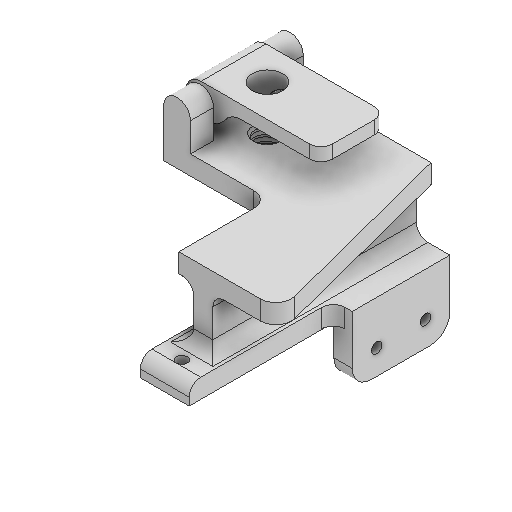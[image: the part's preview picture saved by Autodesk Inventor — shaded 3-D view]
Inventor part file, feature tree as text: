
AUTODESK INVENTOR PART (.ipt)
format: ipt  version: 2025 (Build 290162000, 162)  size: 534,016 bytes
history: native  units: mm
features: sketch x20, extrude x19, projected_geometry x18, fillet x7, plane x6, mirror x1, helix x1
ambient origin geometry x8: Origin, YZ Plane, XZ Plane, XY Plane, X Axis, Y Axis, Z Axis, Center Point
bodies: Solid1 (feature_tree)
feature tree (72):
  extrude  "Extrusion1"  Depth=152.4mm
  plane  "Work Plane1"
  extrude  "Extrusion2"  [1 undecoded]
  extrude  "Extrusion3"  Depth=0.25mm
  extrude  "Extrusion4"  Depth=25.4mm
  fillet  "Fillet1"  Radius=2.75mm
  extrude  "Extrusion5"  Depth=10.0mm TaperAngle=0.0deg
  extrude  "Extrusion6"  Depth=10.0mm
  extrude  "Extrusion7"  Depth=10.0mm TaperAngle=0.0deg
  extrude  "Extrusion8"  Depth=10.0mm TaperAngle=0.0deg
  extrude  "Extrusion9"  Depth=25.4mm TaperAngle=0.0deg
  extrude  "Extrusion10"  Depth=14.0mm
  extrude  "Extrusion11"  Depth=8.0mm
  plane  "Work Plane2"
  extrude  "Extrusion12"  Depth=15.0mm
  mirror  "Mirror1"
  plane  "Work Plane3"
  sketch  "Sketch13"  dims[d37=0.5mm d38=0.5mm]
  plane  "Work Plane4"
  extrude  "Extrusion13"  Depth=0.5mm
  extrude  "Extrusion14"  Depth=10.0mm
  fillet  "Fillet2"  Radius=55.0mm
  fillet  "Fillet3"  [1 undecoded]
  fillet  "Fillet4"  Radius=10.0mm
  extrude  "Extrusion15"  Depth=6.0mm
  extrude  "Extrusion16"  TaperAngle=0.0deg  [1 undecoded]
  fillet  "Fillet5"  Radius=1.5mm
  extrude  "Extrusion17"  Depth=6.0mm
  extrude  "Extrusion18"  Depth=6.0mm TaperAngle=0.0deg
  fillet  "Fillet6"  Radius=6.0mm
  fillet  "Fillet7"  Radius=6.0mm
  plane  "Work Plane5"
  helix  "Coil2"  [1 undecoded]
  plane  "Work Plane6"
  extrude  "Extrusion19"  Depth=10.0mm
  sketch  "Sketch1"  dims[d0=25.4mm d1=152.4mm]
  sketch  "Sketch2"  dims[d2=10.0mm d3=0.0mm d4=-50.8mm]
  projected_geometry  "Projected Loop1"
  sketch  "Sketch3"  dims[d5=25.4mm d6=0.25mm]
  projected_geometry  "Projected Loop2"
  sketch  "Sketch4"  dims[d7=50.8mm d8=0.0mm d9=25.4mm d10=2.75mm]
  sketch  "Sketch5"  dims[d11=35.45mm d12=0.0mm d13=10.0mm d14=0.0mm]
  projected_geometry  "Projected Loop3"
  sketch  "Sketch6"  dims[d15=10.0mm d16=55.0mm]
  projected_geometry  "Projected Loop4"
  sketch  "Sketch7"  dims[d17=55.0mm d18=10.0mm d19=0.0mm]
  projected_geometry  "Projected Loop5"
  sketch  "Sketch8"  dims[d20=0.0mm d21=0.0mm d22=10.0mm d23=0.0mm]
  projected_geometry  "Projected Loop6"
  sketch  "Sketch9"  dims[d24=25.4mm d25=0.0mm d26=25.4mm d27=0.0mm]
  projected_geometry  "Projected Loop7"
  sketch  "Sketch10"  dims[d28=55.0mm d29=0.0mm d30=14.0mm]
  projected_geometry  "Projected Loop8"
  sketch  "Sketch11"  dims[d31=12.0mm d32=0.0mm d33=8.0mm]
  projected_geometry  "Projected Loop9"
  sketch  "Sketch12"  dims[d34=12.0mm d35=0.0mm d36=15.0mm]
  projected_geometry  "Projected Loop10"
  projected_geometry  "Projected Loop11"
  sketch  "Sketch14"  dims[d39=16.0mm d40=0.5mm d41=55.0mm d42=0.0mm d43=0.0mm d44=0.0mm d45=10.0mm]
  projected_geometry  "Projected Loop12"
  sketch  "Sketch15"  dims[d46=8.0mm d47=6.0mm]
  projected_geometry  "Projected Loop13"
  sketch  "Sketch16"  dims[d48=12.7mm d49=0.0mm d50=0.0mm d53=1.5mm]
  sketch  "Sketch17"  dims[d54=15.0mm d55=0.0mm d56=6.0mm]
  projected_geometry  "Projected Loop14"
  sketch  "Sketch18"  dims[d57=20.0mm d58=0.0mm d59=20.0mm d60=0.0mm d61=6.0mm d62=6.0mm d71=2.0mm]
  projected_geometry  "Projected Loop15"
  sketch  "Sketch19"  dims[d72=3.0mm d73=10.0mm d74=50.0mm d75=0.0mm d76=90.0deg d77=90.0deg d78=0.0mm d79=0.0mm d80=6.35mm]
  projected_geometry  "Projected Loop16"
  sketch  "Sketch20"  dims[d81=61.0mm d82=2.5mm d83=2.5mm d84=0.0mm d85=0.0mm]
  projected_geometry  "Projected Loop17"
  projected_geometry  "Projected Loop18"
note: 4 required parameter values undecoded (feature->parameter linkage not recoverable at this tier; creation-order binding heuristic only, values carry confidence <= 0.55)
